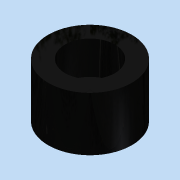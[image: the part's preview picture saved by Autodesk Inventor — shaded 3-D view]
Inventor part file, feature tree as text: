
AUTODESK INVENTOR PART (.ipt)
format: ipt  version: 2015 (Build 190159000, 159)  size: 90,112 bytes
history: native  units: in
note: dims shown in document units (in); Inventor stores cm internally (conversion verified against a paired STEP export)
features: extrude x2, sketch x2
ambient origin geometry x8: Origin, YZ Plane, XZ Plane, XY Plane, X Axis, Y Axis, Z Axis, Center Point
bodies: Solid1 (feature_tree)
feature tree (4):
  extrude  "Extrusion1"  Depth=0.1875in
  extrude  "Extrusion2"  Depth=0.0787in TaperAngle=0.0deg
  sketch  "Sketch1"  dims[d0=0.315in d1=0.1875in]
  sketch  "Sketch2"  dims[d2=0.125in d3=0.0in d4=0.0787in d5=0.0in]
